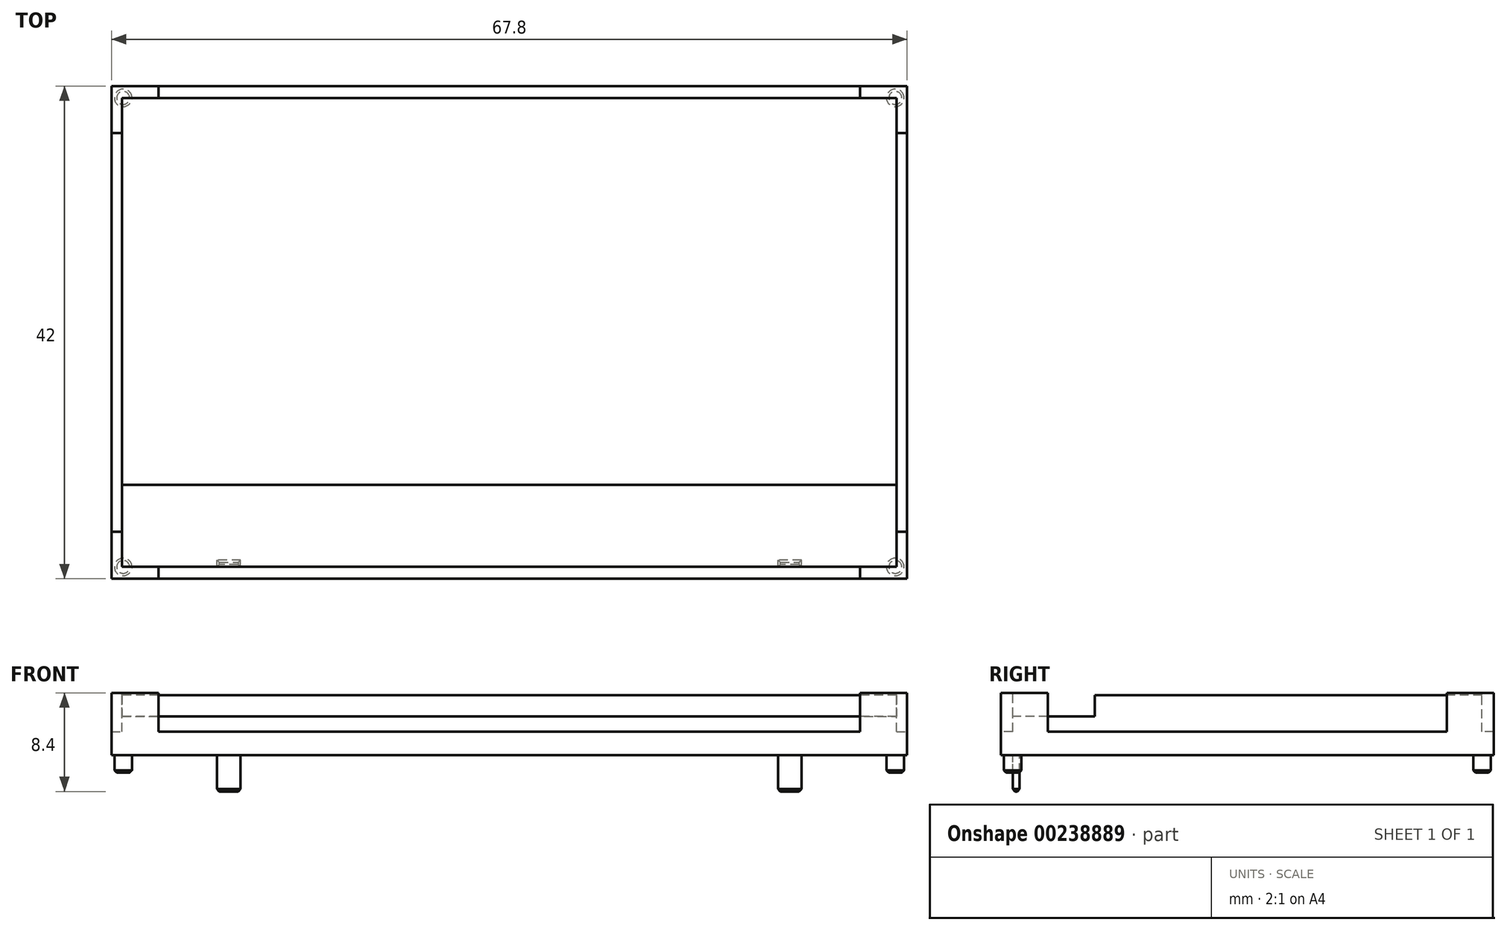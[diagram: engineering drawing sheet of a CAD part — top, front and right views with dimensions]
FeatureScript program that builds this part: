
annotation { "Feature Type Name" : "Feature", "Feature Type Description" : "" }
export const myFeature = defineFeature(function(context is Context, id is Id, definition is map)
    precondition{}
    {
        {
            var Q0;
            Q0=qCreatedBy(makeId("Top.planeOp"),FACE);
            var sketch = newSketch(context, id + "F0", { "sketchPlane" : qUnion([Q0])});
            skLineSegment(sketch, "E0.bottom", {"start": v(33.9, 21) * mm, "end": v(-33.9, 21) * mm});
            skLineSegment(sketch, "E0.top", {"start": v(33.9, -21) * mm, "end": v(-33.9, -21) * mm});
            skLineSegment(sketch, "E0.left", {"start": v(33.9, 21) * mm, "end": v(33.9, -21) * mm});
            skLineSegment(sketch, "E0.right", {"start": v(-33.9, 21) * mm, "end": v(-33.9, -21) * mm});
            skPoint(sketch, "E0.middle", {"position": v(0, 0) * mm});
            skCircle(sketch, "E1", {"center": v(-32.9, 20) * mm, "radius": 0.75 * mm});
            skCircle(sketch, "E2", {"center": v(32.9, 20) * mm, "radius": 0.75 * mm});
            skCircle(sketch, "E3", {"center": v(32.9, -20) * mm, "radius": 0.75 * mm});
            skCircle(sketch, "E4", {"center": v(-32.9, -20) * mm, "radius": 0.75 * mm});
            skLineSegment(sketch, "E5.bottom", {"start": v(-22.9, -20) * mm, "end": v(-24.9, -20) * mm});
            skLineSegment(sketch, "E5.top", {"start": v(-22.9, -19.4) * mm, "end": v(-24.9, -19.4) * mm});
            skLineSegment(sketch, "E5.left", {"start": v(-22.9, -20) * mm, "end": v(-22.9, -19.4) * mm});
            skLineSegment(sketch, "E5.right", {"start": v(-24.9, -20) * mm, "end": v(-24.9, -19.4) * mm});
            skPoint(sketch, "E5.middle", {"position": v(-23.9, -19.7) * mm});
            skLineSegment(sketch, "E6.bottom", {"start": v(24.9, -20) * mm, "end": v(22.9, -20) * mm});
            skLineSegment(sketch, "E6.top", {"start": v(24.9, -19.4) * mm, "end": v(22.9, -19.4) * mm});
            skLineSegment(sketch, "E6.left", {"start": v(24.9, -20) * mm, "end": v(24.9, -19.4) * mm});
            skLineSegment(sketch, "E6.right", {"start": v(22.9, -20) * mm, "end": v(22.9, -19.4) * mm});
            skPoint(sketch, "E6.middle", {"position": v(23.9, -19.7) * mm});
            skSolve(sketch);
        }
        {
            var Q0;
            Q0=makeQuery(id+"F0.imprint","IMPRINT",FACE,{"disambiguationData":[TD([[makeQuery(id+"F0.imprint","IMPRINT",EDGE,{"derivedFrom":sQuery(id+"F0.wireOp",EDGE,"E0.bottom")}),1.0]])]});
            var Q1;
            Q1=makeQuery(id+"F0.imprint","IMPRINT",FACE,{"disambiguationData":[TD([[makeQuery(id+"F0.imprint","IMPRINT",EDGE,{"derivedFrom":sQuery(id+"F0.wireOp",EDGE,"E2")}),1.0]])]});
            var Q2;
            Q2=makeQuery(id+"F0.imprint","IMPRINT",FACE,{"disambiguationData":[TD([[makeQuery(id+"F0.imprint","IMPRINT",EDGE,{"derivedFrom":sQuery(id+"F0.wireOp",EDGE,"E3")}),1.0]])]});
            var Q3;
            Q3=makeQuery(id+"F0.imprint","IMPRINT",FACE,{"disambiguationData":[TD([[makeQuery(id+"F0.imprint","IMPRINT",EDGE,{"derivedFrom":sQuery(id+"F0.wireOp",EDGE,"E1")}),1.0]])]});
            var Q4;
            Q4=makeQuery(id+"F0.imprint","IMPRINT",FACE,{"disambiguationData":[TD([[makeQuery(id+"F0.imprint","IMPRINT",EDGE,{"derivedFrom":sQuery(id+"F0.wireOp",EDGE,"E4")}),1.0]])]});
            var Q5;
            Q5=makeQuery(id+"F0.imprint","IMPRINT",FACE,{"disambiguationData":[TD([[makeQuery(id+"F0.imprint","IMPRINT",EDGE,{"derivedFrom":sQuery(id+"F0.wireOp",EDGE,"E5.bottom")}),-1.0]])]});
            var Q6;
            Q6=makeQuery(id+"F0.imprint","IMPRINT",FACE,{"disambiguationData":[TD([[makeQuery(id+"F0.imprint","IMPRINT",EDGE,{"derivedFrom":sQuery(id+"F0.wireOp",EDGE,"E6.bottom")}),-1.0]])]});
            extrude(context, id + "F1", {"entities" : qUnion([Q0, Q1, Q2, Q3, Q4, Q5, Q6]), "depth" : 5.3 * mm});
        }
        {
            var Q0;
            Q0=makeQuery(id+"F0.imprint","IMPRINT",FACE,{"disambiguationData":[TD([[makeQuery(id+"F0.imprint","IMPRINT",EDGE,{"derivedFrom":sQuery(id+"F0.wireOp",EDGE,"E4")}),1.0]])]});
            var Q1;
            Q1=makeQuery(id+"F0.imprint","IMPRINT",FACE,{"disambiguationData":[TD([[makeQuery(id+"F0.imprint","IMPRINT",EDGE,{"derivedFrom":sQuery(id+"F0.wireOp",EDGE,"E3")}),1.0]])]});
            var Q2;
            Q2=makeQuery(id+"F0.imprint","IMPRINT",FACE,{"disambiguationData":[TD([[makeQuery(id+"F0.imprint","IMPRINT",EDGE,{"derivedFrom":sQuery(id+"F0.wireOp",EDGE,"E2")}),1.0]])]});
            var Q3;
            Q3=makeQuery(id+"F0.imprint","IMPRINT",FACE,{"disambiguationData":[TD([[makeQuery(id+"F0.imprint","IMPRINT",EDGE,{"derivedFrom":sQuery(id+"F0.wireOp",EDGE,"E1")}),1.0]])]});
            extrude(context, id + "F2", {"entities" : qUnion([Q0, Q1, Q2, Q3]), "operationType" : NewBodyOperationType.ADD, "oppositeDirection" : true, "depth" : 1.5 * mm});
        }
        {
            var Q0;
            Q0=makeQuery(id+"F0.imprint","IMPRINT",FACE,{"disambiguationData":[TD([[makeQuery(id+"F0.imprint","IMPRINT",EDGE,{"derivedFrom":sQuery(id+"F0.wireOp",EDGE,"E5.bottom")}),-1.0]])]});
            var Q1;
            Q1=makeQuery(id+"F0.imprint","IMPRINT",FACE,{"disambiguationData":[TD([[makeQuery(id+"F0.imprint","IMPRINT",EDGE,{"derivedFrom":sQuery(id+"F0.wireOp",EDGE,"E6.bottom")}),-1.0]])]});
            extrude(context, id + "F3", {"entities" : qUnion([Q0, Q1]), "operationType" : NewBodyOperationType.ADD, "oppositeDirection" : true, "depth" : 3.1 * mm});
        }
        {
            var Q0;
            Q0=makeQuery(id+"F1.opExtrude","CAP_FACE",FACE,{"disambiguationData":[OSD([sQuery(id+"F0.wireOp",EDGE,"E0.bottom"),sQuery(id+"F0.wireOp",EDGE,"E0.top"),sQuery(id+"F0.wireOp",EDGE,"E0.left"),sQuery(id+"F0.wireOp",EDGE,"E0.right")])],"isStart":false});
            var sketch = newSketch(context, id + "F4", { "sketchPlane" : qUnion([Q0])});
            skLineSegment(sketch, "E7.bottom", {"start": v(33, 20) * mm, "end": v(29.9, 20) * mm});
            skLineSegment(sketch, "E7.top", {"start": v(33, -20) * mm, "end": v(29.9, -20) * mm});
            skLineSegment(sketch, "E7.left", {"start": v(33, 20) * mm, "end": v(33, 17) * mm});
            skLineSegment(sketch, "E7.right", {"start": v(-33, 20) * mm, "end": v(-33, 17) * mm});
            skPoint(sketch, "E7.middle", {"position": v(0, 0) * mm});
            skLineSegment(sketch, "E8", {"start": v(-33.9, 17) * mm, "end": v(-33, 17) * mm});
            skLineSegment(sketch, "E9", {"start": v(-29.9, 21) * mm, "end": v(-29.9, 20) * mm});
            skLineSegment(sketch, "E10", {"start": v(-33.9, -17) * mm, "end": v(-33, -17) * mm});
            skLineSegment(sketch, "E11", {"start": v(-29.9, -20) * mm, "end": v(-29.9, -21) * mm});
            skLineSegment(sketch, "E12", {"start": v(29.9, 21) * mm, "end": v(29.9, 20) * mm});
            skLineSegment(sketch, "E13", {"start": v(33, 17) * mm, "end": v(33.9, 17) * mm});
            skLineSegment(sketch, "E14", {"start": v(29.9, -20) * mm, "end": v(29.9, -21) * mm});
            skLineSegment(sketch, "E15", {"start": v(33, -17) * mm, "end": v(33.9, -17) * mm});
            skLineSegment(sketch, "E16", {"start": v(-33.9, 17) * mm, "end": v(-33.9, -17) * mm});
            skLineSegment(sketch, "E17", {"start": v(-29.9, -21) * mm, "end": v(29.9, -21) * mm});
            skLineSegment(sketch, "E18", {"start": v(33.9, -17) * mm, "end": v(33.9, 17) * mm});
            skLineSegment(sketch, "E19", {"start": v(29.9, 21) * mm, "end": v(-29.9, 21) * mm});
            skLineSegment(sketch, "E20.trimOffspring", {"start": v(-29.9, 20) * mm, "end": v(-33, 20) * mm});
            skLineSegment(sketch, "E21.trimOffspring", {"start": v(-33, -17) * mm, "end": v(-33, -20) * mm});
            skLineSegment(sketch, "E22.trimOffspring", {"start": v(-29.9, -20) * mm, "end": v(-33, -20) * mm});
            skLineSegment(sketch, "E23.trimOffspring", {"start": v(33, -17) * mm, "end": v(33, -20) * mm});
            skSolve(sketch);
        }
        {
            var Q0;
            Q0=makeQuery(id+"F4.imprint","IMPRINT",FACE,{"disambiguationData":[TD([[makeQuery(id+"F4.imprint","IMPRINT",EDGE,{"derivedFrom":sQuery(id+"F4.wireOp",EDGE,"E7.bottom")}),1.0]])]});
            extrude(context, id + "F5", {"entities" : qUnion([Q0]), "operationType" : NewBodyOperationType.REMOVE, "oppositeDirection" : true, "depth" : (5.3 - 2) * mm});
        }
        {
            var Q0;
            Q0=makeQuery(id+"F5.boolean.opBoolean","COPY",FACE,{"derivedFrom":makeQuery(id+"F5.opExtrude","CAP_FACE",FACE,{"disambiguationData":[OSD([sQuery(id+"F4.wireOp",EDGE,"E7.bottom"),sQuery(id+"F4.wireOp",EDGE,"E7.top"),sQuery(id+"F4.wireOp",EDGE,"E7.left"),sQuery(id+"F4.wireOp",EDGE,"E7.right"),sQuery(id+"F4.wireOp",EDGE,"E8"),sQuery(id+"F4.wireOp",EDGE,"E9"),sQuery(id+"F4.wireOp",EDGE,"E10"),sQuery(id+"F4.wireOp",EDGE,"E11"),sQuery(id+"F4.wireOp",EDGE,"E12"),sQuery(id+"F4.wireOp",EDGE,"E13"),sQuery(id+"F4.wireOp",EDGE,"E14"),sQuery(id+"F4.wireOp",EDGE,"E15"),sQuery(id+"F4.wireOp",EDGE,"E16"),sQuery(id+"F4.wireOp",EDGE,"E17"),sQuery(id+"F4.wireOp",EDGE,"E18"),sQuery(id+"F4.wireOp",EDGE,"E19"),sQuery(id+"F4.wireOp",EDGE,"E20.trimOffspring"),sQuery(id+"F4.wireOp",EDGE,"E21.trimOffspring"),sQuery(id+"F4.wireOp",EDGE,"E22.trimOffspring"),sQuery(id+"F4.wireOp",EDGE,"E23.trimOffspring")])],"isStart":false})});
            var sketch = newSketch(context, id + "F6", { "sketchPlane" : qUnion([Q0])});
            skLineSegment(sketch, "E24.bottom", {"start": v(33, 20) * mm, "end": v(-33, 20) * mm});
            skLineSegment(sketch, "E24.top", {"start": v(33, -20) * mm, "end": v(-33, -20) * mm});
            skLineSegment(sketch, "E24.left", {"start": v(33, 20) * mm, "end": v(33, -20) * mm});
            skLineSegment(sketch, "E24.right", {"start": v(-33, 20) * mm, "end": v(-33, -20) * mm});
            skPoint(sketch, "E24.middle", {"position": v(0, 0) * mm});
            skSolve(sketch);
        }
        {
            var Q0;
            {var subQ1=sQuery(id+"F6.wireOp",EDGE,"E24.bottom");var subQ13=makeQuery(id+"F6.imprint","INTERSECT",VERTEX,{"derivedFrom":[makeQuery(id+"F5.boolean.opBoolean","COPY",EDGE,{"derivedFrom":makeQuery(id+"F5.opExtrude","CAP_EDGE",EDGE,{"disambiguationData":[OSD([sQuery(id+"F4.wireOp",EDGE,"E12")])],"isStart":false})}),subQ1]});Q0=makeQuery(id+"F6.imprint","IMPRINT",FACE,{"disambiguationData":[TD([[makeQuery(id+"F6.imprint","IMPRINT",EDGE,{"disambiguationData":[TD([[subQ13,-1.0]])],"derivedFrom":subQ1}),1.0]])]});}
            extrude(context, id + "F7", {"entities" : qUnion([Q0]), "operationType" : NewBodyOperationType.ADD, "depth" : (5.3 - 2 - 2) * mm});
        }
        {
            var Q0;
            Q0=makeQuery(id+"F7.opExtrude","CAP_FACE",FACE,{"disambiguationData":[OSD([sQuery(id+"F6.wireOp",EDGE,"E24.bottom"),sQuery(id+"F6.wireOp",EDGE,"E24.top"),sQuery(id+"F6.wireOp",EDGE,"E24.left"),sQuery(id+"F6.wireOp",EDGE,"E24.right")])],"isStart":false});
            var sketch = newSketch(context, id + "F8", { "sketchPlane" : qUnion([Q0])});
            skLineSegment(sketch, "E25.bottom", {"start": v(-33, 20) * mm, "end": v(33, 20) * mm});
            skLineSegment(sketch, "E25.top", {"start": v(-33, -13) * mm, "end": v(33, -13) * mm});
            skLineSegment(sketch, "E25.left", {"start": v(-33, 20) * mm, "end": v(-33, -13) * mm});
            skLineSegment(sketch, "E25.right", {"start": v(33, 20) * mm, "end": v(33, -13) * mm});
            skSolve(sketch);
        }
        {
            var Q0;
            {var subQ0=sQuery(id+"F8.wireOp",EDGE,"E25.top");Q0=makeQuery(id+"F8.imprint","IMPRINT",FACE,{"disambiguationData":[TD([[makeQuery(id+"F8.imprint","IMPRINT",EDGE,{"derivedFrom":subQ0}),1.0]])]});}
            extrude(context, id + "F9", {"entities" : qUnion([Q0]), "operationType" : NewBodyOperationType.ADD, "depth" : (2 - 0.2) * mm});
        }
        {
            var Q0;
            Q0=makeQuery(id+"F2.opExtrude","CAP_EDGE",EDGE,{"disambiguationData":[OSD([sQuery(id+"F0.wireOp",EDGE,"E4")])],"isStart":false});
            var Q1;
            Q1=makeQuery(id+"F3.opExtrude","CAP_EDGE",EDGE,{"disambiguationData":[OSD([sQuery(id+"F0.wireOp",EDGE,"E5.bottom")])],"isStart":false});
            var Q2;
            Q2=makeQuery(id+"F3.opExtrude","CAP_EDGE",EDGE,{"disambiguationData":[OSD([sQuery(id+"F0.wireOp",EDGE,"E5.left")])],"isStart":false});
            var Q3;
            Q3=makeQuery(id+"F3.opExtrude","CAP_EDGE",EDGE,{"disambiguationData":[OSD([sQuery(id+"F0.wireOp",EDGE,"E5.top")])],"isStart":false});
            var Q4;
            Q4=makeQuery(id+"F3.opExtrude","CAP_EDGE",EDGE,{"disambiguationData":[OSD([sQuery(id+"F0.wireOp",EDGE,"E5.right")])],"isStart":false});
            var Q5;
            Q5=makeQuery(id+"F3.opExtrude","CAP_EDGE",EDGE,{"disambiguationData":[OSD([sQuery(id+"F0.wireOp",EDGE,"E6.top")])],"isStart":false});
            var Q6;
            Q6=makeQuery(id+"F3.opExtrude","CAP_EDGE",EDGE,{"disambiguationData":[OSD([sQuery(id+"F0.wireOp",EDGE,"E6.right")])],"isStart":false});
            var Q7;
            Q7=makeQuery(id+"F3.opExtrude","CAP_EDGE",EDGE,{"disambiguationData":[OSD([sQuery(id+"F0.wireOp",EDGE,"E6.bottom")])],"isStart":false});
            var Q8;
            Q8=makeQuery(id+"F3.opExtrude","CAP_EDGE",EDGE,{"disambiguationData":[OSD([sQuery(id+"F0.wireOp",EDGE,"E6.left")])],"isStart":false});
            var Q9;
            Q9=makeQuery(id+"F2.opExtrude","CAP_EDGE",EDGE,{"disambiguationData":[OSD([sQuery(id+"F0.wireOp",EDGE,"E3")])],"isStart":false});
            var Q10;
            Q10=makeQuery(id+"F2.opExtrude","CAP_EDGE",EDGE,{"disambiguationData":[OSD([sQuery(id+"F0.wireOp",EDGE,"E2")])],"isStart":false});
            var Q11;
            Q11=makeQuery(id+"F2.opExtrude","CAP_FACE",FACE,{"disambiguationData":[OSD([sQuery(id+"F0.wireOp",EDGE,"E1")])],"isStart":false});
            chamfer(context, id + "F10", {"entities" : qUnion([Q0, Q1, Q2, Q3, Q4, Q5, Q6, Q7, Q8, Q9, Q10, Q11]), "width" : 0.2 * mm, "tangentPropagation" : true});
        }
    });
